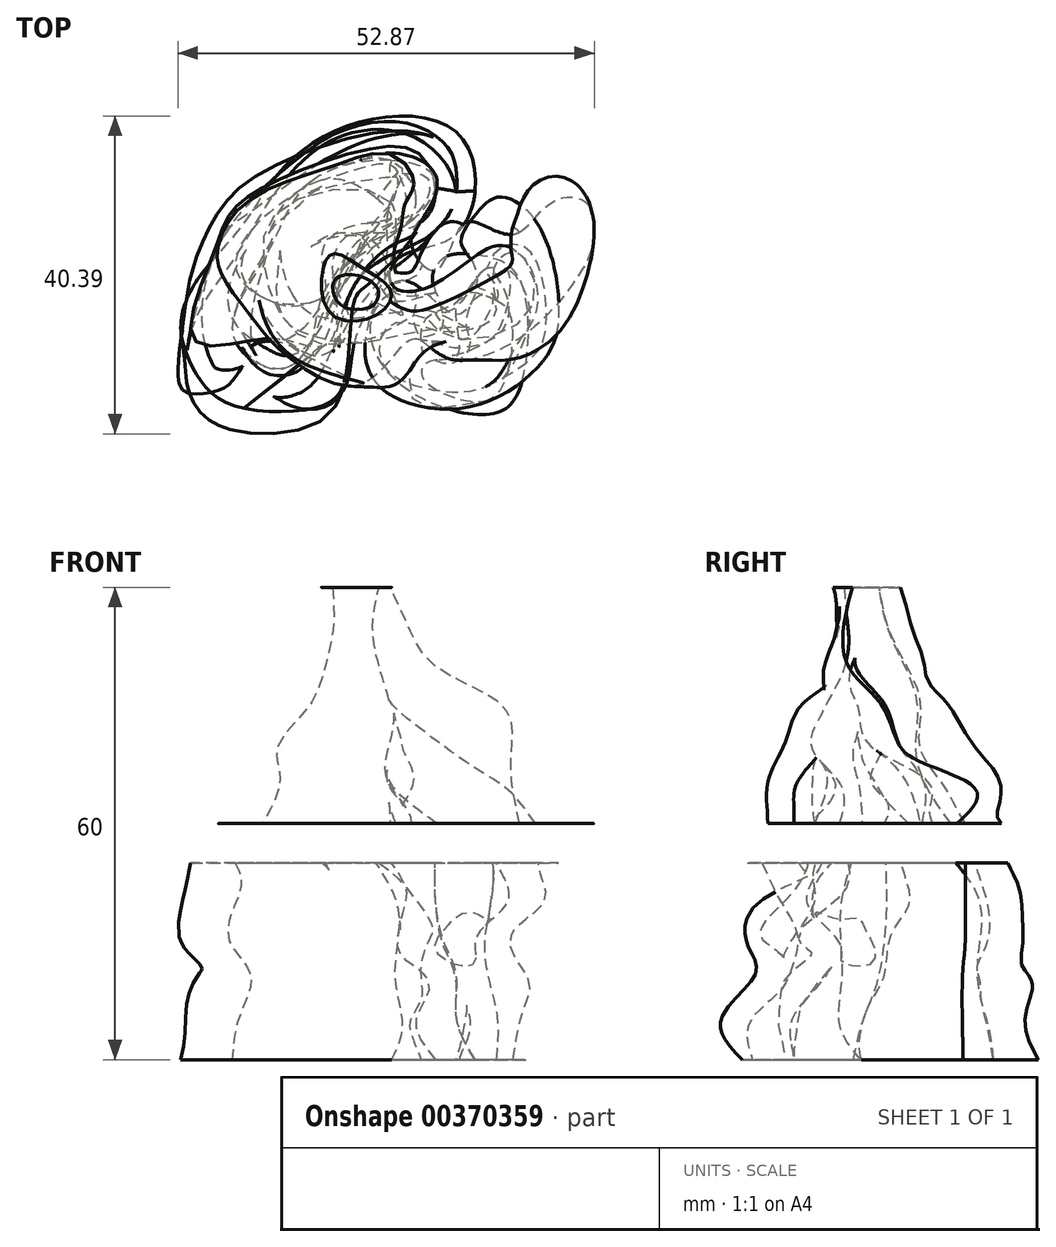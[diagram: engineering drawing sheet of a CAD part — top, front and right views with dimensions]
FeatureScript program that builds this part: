
annotation { "Feature Type Name" : "Feature", "Feature Type Description" : "" }
export const myFeature = defineFeature(function(context is Context, id is Id, definition is map)
    precondition{}
    {
        {
            var Q0;
            Q0=qCreatedBy(makeId("Top.planeOp"),FACE);
            cPlane(context, id + "F0", {"entities" : qUnion([Q0]), "cplaneType" : CPlaneType.OFFSET, "offset" : 5 * mm, "width" : 152.4 * mm, "height" : 152.4 * mm});
        }
        {
            var Q0;
            Q0=qCreatedBy(id+"F0.planeOp",FACE);
            var sketch = newSketch(context, id + "F1", { "sketchPlane" : qUnion([Q0])});
            skFitSpline(sketch, "E0", {"points": [v(10.66, 15.7) * mm, v(7.94, 23.44) * mm, v(-3.49, 24.6) * mm, v(-13.56, 18.8) * mm, v(-19.18, 11.04) * mm, v(-24.6, 4.46) * mm, v(-26.73, -1.55) * mm, v(-25, -7.17) * mm, v(-20.34, -11.43) * mm, v(-8.91, -11.62) * mm, v(-5.81, -7.94) * mm, v(-4.65, 1.94) * mm, v(-3.1, 3.68) * mm, v(1.55, 7.56) * mm, v(7.56, 9.69) * mm, v(10.66, 15.7) * mm]});
            skSolve(sketch);
        }
        {
            var Q0;
            Q0=qCreatedBy(id+"F0.planeOp",FACE);
            var sketch = newSketch(context, id + "F2", { "sketchPlane" : qUnion([Q0])});
            skFitSpline(sketch, "E1", {"points": [v(0, 2.71) * mm, v(-2.71, -1.94) * mm, v(1.74, -9.3) * mm, v(12.98, -12.6) * mm, v(16.66, -8.33) * mm, v(16.66, 3.68) * mm, v(13.95, 6.78) * mm, v(10.85, 7.56) * mm, v(6.97, 7.36) * mm, v(5.23, 4.84) * mm, v(6, 1.94) * mm, v(6.4, -1.74) * mm, v(4.84, -2.71) * mm, v(3.68, -2.71) * mm, v(2.9, 0) * mm, v(3.1, 2.71) * mm, v(0, 2.71) * mm]});
            skSolve(sketch);
        }
        {
            var Q0;
            Q0=qCreatedBy(id+"F0.planeOp",FACE);
            var sketch = newSketch(context, id + "F3", { "sketchPlane" : qUnion([Q0])});
            skFitSpline(sketch, "E2", {"points": [v(0, 19.57) * mm, v(-10.46, 16.66) * mm, v(-15.7, 7.94) * mm, v(-20.15, -2.32) * mm, v(-15.5, -6.78) * mm, v(-11.82, -5.81) * mm, v(-8.72, 0) * mm, v(-4.26, 8.14) * mm, v(2.13, 11.62) * mm, v(5.62, 17.05) * mm, v(0, 19.57) * mm]});
            skSolve(sketch);
        }
        {
            var Q0;
            Q0=qCreatedBy(id+"F0.planeOp",FACE);
            var sketch = newSketch(context, id + "F4", { "sketchPlane" : qUnion([Q0])});
            skFitSpline(sketch, "E3", {"points": [v(13.37, 1.74) * mm, v(9.5, 2.71) * mm, v(8.14, 0) * mm, v(8.33, -5.23) * mm, v(4.84, -6) * mm, v(3.87, -7.75) * mm, v(8.33, -10.66) * mm, v(12.98, -10.46) * mm, v(15.11, -6) * mm, v(15.11, 0) * mm, v(13.37, 1.74) * mm]});
            skSolve(sketch);
        }
        {
            var Q0;
            Q0=qCreatedBy(id+"F0.planeOp",FACE);
            cPlane(context, id + "F5", {"entities" : qUnion([Q0]), "cplaneType" : CPlaneType.OFFSET, "offset" : 5 * mm, "width" : 152.4 * mm, "height" : 152.4 * mm});
        }
        {
            var Q0;
            Q0=qCreatedBy(id+"F5.planeOp",FACE);
            var sketch = newSketch(context, id + "F6", { "sketchPlane" : qUnion([Q0])});
            skFitSpline(sketch, "E4", {"points": [v(3.1, 22.47) * mm, v(-6.78, 22.47) * mm, v(-14.14, 16.27) * mm, v(-20.15, 6.97) * mm, v(-24.6, 0) * mm, v(-25.96, -8.72) * mm, v(-21.31, -14.34) * mm, v(-8.91, -13.17) * mm, v(-6.78, -6.2) * mm, v(-4.07, 4.46) * mm, v(3.68, 9.3) * mm, v(8.33, 15.3) * mm, v(3.1, 22.47) * mm]});
            skSolve(sketch);
        }
        {
            var Q0;
            Q0=qCreatedBy(id+"F5.planeOp",FACE);
            var sketch = newSketch(context, id + "F7", { "sketchPlane" : qUnion([Q0])});
            skFitSpline(sketch, "E5", {"points": [v(1.74, 0) * mm, v(4.65, -1.74) * mm, v(8.91, 1.94) * mm, v(8.72, 9.3) * mm, v(12.6, 10.85) * mm, v(18.6, 9.5) * mm, v(20.54, 4.84) * mm, v(19.37, 0) * mm, v(16.47, -7.36) * mm, v(13.95, -9.88) * mm, v(6.4, -13.17) * mm, v(2.9, -12.6) * mm, v(0, -11.04) * mm, v(-1.94, -4.65) * mm, v(0, -1.74) * mm, v(1.74, 0) * mm]});
            skSolve(sketch);
        }
        {
            var Q0;
            Q0=qCreatedBy(id+"F5.planeOp",FACE);
            var sketch = newSketch(context, id + "F8", { "sketchPlane" : qUnion([Q0])});
            skFitSpline(sketch, "E6", {"points": [v(-1.95, 18.75) * mm, v(-12.28, 15.24) * mm, v(-14.78, 10.42) * mm, v(-18.5, 3.1) * mm, v(-19.3, -2.81) * mm, v(-16.29, -7.23) * mm, v(-12.38, -7.43) * mm, v(-10.17, -4.72) * mm, v(-8.97, 1.8) * mm, v(-4.46, 7.41) * mm, v(2.56, 12.43) * mm, v(2.56, 16.84) * mm, v(-1.95, 18.75) * mm]});
            skSolve(sketch);
        }
        {
            var Q0;
            Q0=qCreatedBy(id+"F5.planeOp",FACE);
            var sketch = newSketch(context, id + "F9", { "sketchPlane" : qUnion([Q0])});
            skFitSpline(sketch, "E7", {"points": [v(13.5, 3) * mm, v(10.59, 2) * mm, v(9.38, -0.9) * mm, v(9.99, -4.12) * mm, v(6.88, -6.02) * mm, v(4.47, -5.32) * mm, v(2.87, -5.82) * mm, v(2.46, -7.73) * mm, v(3.17, -10.84) * mm, v(9.58, -10.23) * mm, v(15.71, -5.86) * mm, v(15.71, 1.14) * mm, v(13.5, 3) * mm]});
            skSolve(sketch);
        }
        {
            var Q0;
            Q0=qCreatedBy(id+"F5.planeOp",FACE);
            cPlane(context, id + "F10", {"entities" : qUnion([Q0]), "cplaneType" : CPlaneType.OFFSET, "offset" : 5 * mm, "width" : 152.4 * mm, "height" : 152.4 * mm});
        }
        {
            var Q0;
            Q0=qCreatedBy(id+"F10.planeOp",FACE);
            var sketch = newSketch(context, id + "F11", { "sketchPlane" : qUnion([Q0])});
            skFitSpline(sketch, "E8", {"points": [v(-8.91, 21.9) * mm, v(2.9, 24.02) * mm, v(7.75, 19.95) * mm, v(7.17, 12.6) * mm, v(0, 5.62) * mm, v(-3.1, 2.32) * mm, v(-6.97, -3.49) * mm, v(-10.46, -9.5) * mm, v(-18.21, -11.04) * mm, v(-24.4, -7.17) * mm, v(-24.02, 2.9) * mm, v(-21.9, 8.91) * mm, v(-19.57, 12.2) * mm, v(-8.91, 21.9) * mm]});
            skSolve(sketch);
        }
        {
            var Q0;
            Q0=qCreatedBy(id+"F10.planeOp",FACE);
            var sketch = newSketch(context, id + "F12", { "sketchPlane" : qUnion([Q0])});
            skFitSpline(sketch, "E9", {"points": [v(0, -2.13) * mm, v(1.74, 2.13) * mm, v(3.87, 2.52) * mm, v(7.36, 2.13) * mm, v(9.88, 5.81) * mm, v(12.98, 7.56) * mm, v(16.85, 6.97) * mm, v(18.21, 3.1) * mm, v(18.4, -1.55) * mm, v(16.27, -4.84) * mm, v(12.2, -6.97) * mm, v(8.91, -7.75) * mm, v(4.26, -8.14) * mm, v(1.55, -5.62) * mm, v(0, -2.13) * mm]});
            skSolve(sketch);
        }
        {
            var Q0;
            Q0=qCreatedBy(id+"F10.planeOp",FACE);
            var sketch = newSketch(context, id + "F13", { "sketchPlane" : qUnion([Q0])});
            skFitSpline(sketch, "E10", {"points": [v(14.7, 5.4) * mm, v(11.29, 4) * mm, v(10.09, 2.3) * mm, v(6.68, -2.41) * mm, v(4.17, -2.31) * mm, v(3.87, -4.02) * mm, v(6.07, -6.32) * mm, v(13.6, -5.72) * mm, v(16.9, -2.41) * mm, v(17.4, 1.7) * mm, v(14.7, 5.4) * mm]});
            skSolve(sketch);
        }
        {
            var Q0;
            Q0=qCreatedBy(id+"F10.planeOp",FACE);
            var sketch = newSketch(context, id + "F14", { "sketchPlane" : qUnion([Q0])});
            skFitSpline(sketch, "E11", {"points": [v(-0.95, 17.44) * mm, v(-13.38, 14.13) * mm, v(-15.29, 9.52) * mm, v(-17.8, -1.1) * mm, v(-15.49, -6.93) * mm, v(-8.77, -3.01) * mm, v(-5.46, 7.72) * mm, v(0, 11.53) * mm, v(3.87, 13.93) * mm, v(4.57, 17.24) * mm, v(-0.95, 17.44) * mm]});
            skSolve(sketch);
        }
        {
            var Q0;
            Q0=qCreatedBy(id+"F10.planeOp",FACE);
            cPlane(context, id + "F15", {"entities" : qUnion([Q0]), "cplaneType" : CPlaneType.OFFSET, "offset" : 5 * mm, "width" : 152.4 * mm, "height" : 152.4 * mm});
        }
        {
            var Q0;
            Q0=qCreatedBy(id+"F15.planeOp",FACE);
            var sketch = newSketch(context, id + "F16", { "sketchPlane" : qUnion([Q0])});
            skFitSpline(sketch, "E12", {"points": [v(-17.05, 13.75) * mm, v(-5.81, 21.31) * mm, v(5.62, 21.9) * mm, v(4.84, 11.82) * mm, v(0, 8.72) * mm, v(-4.65, 3.68) * mm, v(-7.17, -3.87) * mm, v(-8.14, -10.07) * mm, v(-10.07, -11.62) * mm, v(-13.17, -11.43) * mm, v(-15.3, -8.91) * mm, v(-15.89, -6.78) * mm, v(-18.6, -6.4) * mm, v(-20.54, -8.52) * mm, v(-22.09, -9.3) * mm, v(-25.18, -9.5) * mm, v(-26.54, -8.72) * mm, v(-26.35, -2.71) * mm, v(-24.22, 7.36) * mm, v(-17.05, 13.75) * mm]});
            skSolve(sketch);
        }
        {
            var Q0;
            Q0=qCreatedBy(id+"F15.planeOp",FACE);
            var sketch = newSketch(context, id + "F17", { "sketchPlane" : qUnion([Q0])});
            skFitSpline(sketch, "E13", {"points": [v(0, 18.6) * mm, v(-12.7, 13.89) * mm, v(-15.9, 9.73) * mm, v(-20.33, 2.38) * mm, v(-19.78, -1.22) * mm, v(-16.31, -4) * mm, v(-11.74, -4.68) * mm, v(-4.67, 7.23) * mm, v(0, 14.02) * mm, v(0, 18.6) * mm]});
            skSolve(sketch);
        }
        {
            var Q0;
            Q0=qCreatedBy(id+"F15.planeOp",FACE);
            var sketch = newSketch(context, id + "F18", { "sketchPlane" : qUnion([Q0])});
            skFitSpline(sketch, "E14", {"points": [v(14.6, 5.85) * mm, v(11.4, 5.3) * mm, v(9.32, 1.83) * mm, v(5.72, 0) * mm, v(4.75, -3.02) * mm, v(6.7, -5.24) * mm, v(11.54, -3.85) * mm, v(13.9, -1.5) * mm, v(14.6, 5.85) * mm]});
            skSolve(sketch);
        }
        {
            var Q0;
            Q0=qCreatedBy(id+"F15.planeOp",FACE);
            cPlane(context, id + "F19", {"entities" : qUnion([Q0]), "cplaneType" : CPlaneType.OFFSET, "offset" : 5 * mm, "width" : 152.4 * mm, "height" : 152.4 * mm});
        }
        {
            var Q0;
            Q0=qCreatedBy(id+"F19.planeOp",FACE);
            var sketch = newSketch(context, id + "F20", { "sketchPlane" : qUnion([Q0])});
            skFitSpline(sketch, "E15", {"points": [v(0, -2.9) * mm, v(2.13, 2.32) * mm, v(6.97, -1.74) * mm, v(10.27, -2.71) * mm, v(13.17, 2.32) * mm, v(11.62, 3.49) * mm, v(8.78, 5.55) * mm, v(7.73, 7.13) * mm, v(10.2, 11.79) * mm, v(15.4, 12.24) * mm, v(18.99, 10.07) * mm, v(21.31, 3.87) * mm, v(21.5, -4.26) * mm, v(17.24, -7.75) * mm, v(10.46, -8.72) * mm, v(3.68, -8.72) * mm, v(0, -7.56) * mm, v(0, -2.9) * mm]});
            skSolve(sketch);
        }
        {
            var Q0;
            Q0=qCreatedBy(id+"F19.planeOp",FACE);
            var sketch = newSketch(context, id + "F21", { "sketchPlane" : qUnion([Q0])});
            skFitSpline(sketch, "E16", {"points": [v(-25.96, -5.81) * mm, v(-22.09, -6.97) * mm, v(-18.6, -4.84) * mm, v(-16.47, -3.3) * mm, v(-13.37, -3.87) * mm, v(-12.79, -6.4) * mm, v(-11.82, -9.3) * mm, v(-7.56, -10.07) * mm, v(-5.42, -7.94) * mm, v(-4.65, -3.3) * mm, v(0, 6) * mm, v(1.55, 8.33) * mm, v(5.62, 15.89) * mm, v(2.32, 22.28) * mm, v(-4.26, 22.67) * mm, v(-15.5, 18.21) * mm, v(-22.09, 12.79) * mm, v(-25.57, 2.71) * mm, v(-25.96, -5.81) * mm]});
            skSolve(sketch);
        }
        {
            var Q0;
            Q0=qCreatedBy(id+"F19.planeOp",FACE);
            var sketch = newSketch(context, id + "F22", { "sketchPlane" : qUnion([Q0])});
            skFitSpline(sketch, "E17", {"points": [v(0, 18.32) * mm, v(-8.7, 16.52) * mm, v(-12.3, 13.47) * mm, v(-17.28, 9.87) * mm, v(-19.5, 3.08) * mm, v(-14.37, 0) * mm, v(-8.7, 0) * mm, v(-3.15, 9.17) * mm, v(1.56, 13.05) * mm, v(0, 18.32) * mm]});
            skSolve(sketch);
        }
        {
            var Q0;
            Q0=qCreatedBy(id+"F19.planeOp",FACE);
            var sketch = newSketch(context, id + "F23", { "sketchPlane" : qUnion([Q0])});
            skFitSpline(sketch, "E18", {"points": [v(12.65, 7.1) * mm, v(13.9, 3.9) * mm, v(14.73, 0) * mm, v(13.2, -2.6) * mm, v(7.8, -4.13) * mm, v(5.44, -3.44) * mm, v(3.78, -4.13) * mm, v(3.92, -6.62) * mm, v(16.8, -5.52) * mm, v(19.44, 0) * mm, v(16.4, 8.76) * mm, v(12.65, 7.1) * mm]});
            skSolve(sketch);
        }
        {
            var Q0;
            Q0=qCreatedBy(id+"F19.planeOp",FACE);
            cPlane(context, id + "F24", {"entities" : qUnion([Q0]), "cplaneType" : CPlaneType.OFFSET, "offset" : 5 * mm, "width" : 152.4 * mm, "height" : 152.4 * mm});
        }
        {
            var Q0;
            Q0=qCreatedBy(id+"F24.planeOp",FACE);
            var sketch = newSketch(context, id + "F25", { "sketchPlane" : qUnion([Q0])});
            skFitSpline(sketch, "E19", {"points": [v(-25, -3.3) * mm, v(-16.66, -3.1) * mm, v(-12.79, -3.68) * mm, v(-9.5, -5.23) * mm, v(-5.62, -2.71) * mm, v(-5.42, 0) * mm, v(-6.97, 3.3) * mm, v(-7.36, 6.78) * mm, v(-6, 9.69) * mm, v(-3.68, 10.46) * mm, v(0, 10.46) * mm, v(5.04, 13.17) * mm, v(4.07, 19.95) * mm, v(-2.32, 21.12) * mm, v(-15.3, 16.66) * mm, v(-20.34, 12.98) * mm, v(-22.67, 7.56) * mm, v(-25, -3.3) * mm]});
            skSolve(sketch);
        }
        {
            var Q0;
            Q0=qCreatedBy(id+"F24.planeOp",FACE);
            var sketch = newSketch(context, id + "F26", { "sketchPlane" : qUnion([Q0])});
            skFitSpline(sketch, "E20", {"points": [v(2.9, 3.87) * mm, v(0, 3.87) * mm, v(-2.09, 1.21) * mm, v(-3.3, -5.42) * mm, v(0, -10.27) * mm, v(10.46, -11.62) * mm, v(19.18, -6) * mm, v(21.31, 0) * mm, v(18.4, 11.82) * mm, v(13.56, 14.92) * mm, v(10.66, 12.61) * mm, v(8.86, 9.23) * mm, v(10.46, 6.4) * mm, v(10.46, 2.13) * mm, v(8.14, 0) * mm, v(2.9, 3.87) * mm]});
            skSolve(sketch);
        }
        {
            var Q0;
            Q0=qCreatedBy(id+"F24.planeOp",FACE);
            var sketch = newSketch(context, id + "F27", { "sketchPlane" : qUnion([Q0])});
            skFitSpline(sketch, "E21", {"points": [v(-6.2, 17.07) * mm, v(-12.7, 15) * mm, v(-17.56, 10.98) * mm, v(-19.64, 5.3) * mm, v(-14.1, 1.28) * mm, v(-11.18, 1.28) * mm, v(-8.41, 2.8) * mm, v(-8.7, 8.2) * mm, v(-3.84, 11.53) * mm, v(0, 12.36) * mm, v(-6.2, 17.07) * mm]});
            skSolve(sketch);
        }
        {
            var Q0;
            Q0=qCreatedBy(id+"F24.planeOp",FACE);
            var sketch = newSketch(context, id + "F28", { "sketchPlane" : qUnion([Q0])});
            skFitSpline(sketch, "E22", {"points": [v(15.98, 7.79) * mm, v(12.93, 5.57) * mm, v(13.2, 0) * mm, v(10.02, -1.91) * mm, v(5.72, -2.05) * mm, v(0, -1.22) * mm, v(-1.48, -5.24) * mm, v(2.12, -8.7) * mm, v(12.1, -9.12) * mm, v(15.84, -4) * mm, v(18.6, 1.28) * mm, v(15.98, 7.79) * mm]});
            skSolve(sketch);
        }
        {
            var Q0;
            Q0=qCreatedBy(id+"F24.planeOp",FACE);
            cPlane(context, id + "F29", {"entities" : qUnion([Q0]), "cplaneType" : CPlaneType.OFFSET, "offset" : 5 * mm, "width" : 152.4 * mm, "height" : 152.4 * mm});
        }
        {
            var Q0;
            Q0=qCreatedBy(id+"F29.planeOp",FACE);
            var sketch = newSketch(context, id + "F30", { "sketchPlane" : qUnion([Q0])});
            skFitSpline(sketch, "E23", {"points": [v(16.27, 10.46) * mm, v(20.54, 14.34) * mm, v(24.8, 14.14) * mm, v(25.57, 8.91) * mm, v(23.44, 4.46) * mm, v(17.24, -2.32) * mm, v(7.36, -5.62) * mm, v(3.1, -3.1) * mm, v(0, -5.62) * mm, v(-5.23, -9.1) * mm, v(-14.14, -4.46) * mm, v(-18.02, 0) * mm, v(-21.31, 4.65) * mm, v(-22.09, 7.94) * mm, v(-18.02, 14.53) * mm, v(-3.49, 19.76) * mm, v(0, 20.54) * mm, v(5.23, 18.4) * mm, v(5.04, 13.95) * mm, v(2.52, 9.3) * mm, v(5.42, 5.62) * mm, v(8.14, 9.88) * mm, v(9.88, 11.82) * mm, v(13.17, 10.66) * mm, v(16.27, 10.46) * mm]});
            skSolve(sketch);
        }
        {
            var Q0;
            Q0=qCreatedBy(id+"F29.planeOp",FACE);
            var sketch = newSketch(context, id + "F31", { "sketchPlane" : qUnion([Q0])});
            skFitSpline(sketch, "E24", {"points": [v(0, 14.16) * mm, v(-13.54, 13.75) * mm, v(-16.17, 6.13) * mm, v(-11.46, -2.74) * mm, v(-1.48, -2.6) * mm, v(3.78, 0) * mm, v(7.1, -2.74) * mm, v(17.36, 0) * mm, v(16.95, 7.1) * mm, v(12.93, 8.62) * mm, v(5.03, 3.63) * mm, v(0, 4.05) * mm, v(0, 14.16) * mm]});
            skSolve(sketch);
        }
        {
            var Q0;
            Q0=qCreatedBy(id+"F29.planeOp",FACE);
            cPlane(context, id + "F32", {"entities" : qUnion([Q0]), "cplaneType" : CPlaneType.OFFSET, "offset" : 5 * mm, "width" : 152.4 * mm, "height" : 152.4 * mm});
        }
        {
            var Q0;
            Q0=qCreatedBy(id+"F32.planeOp",FACE);
            var sketch = newSketch(context, id + "F33", { "sketchPlane" : qUnion([Q0])});
            skFitSpline(sketch, "E25", {"points": [v(-6.97, 17.82) * mm, v(-15.89, 14.34) * mm, v(-18.4, 7.36) * mm, v(-17.63, 0) * mm, v(-10.66, -5.42) * mm, v(-10.07, -5.62) * mm, v(-1.94, -9.1) * mm, v(1.94, -7.56) * mm, v(4.26, -4.65) * mm, v(8.14, -3.49) * mm, v(13.37, -5.42) * mm, v(19.76, -3.3) * mm, v(23.44, 2.9) * mm, v(24.4, 10.07) * mm, v(21.7, 16.08) * mm, v(18.02, 16.08) * mm, v(15.7, 11.82) * mm, v(14.14, 8.91) * mm, v(11.82, 8.72) * mm, v(10.07, 9.69) * mm, v(6.78, 11.43) * mm, v(3.68, 6.78) * mm, v(3.3, 5.04) * mm, v(0, 4.26) * mm, v(0, 7.56) * mm, v(0, 14.53) * mm, v(2.71, 16.66) * mm, v(0, 20.34) * mm, v(-6.97, 17.82) * mm]});
            skSolve(sketch);
        }
        {
            var Q0;
            Q0=qCreatedBy(id+"F32.planeOp",FACE);
            var sketch = newSketch(context, id + "F34", { "sketchPlane" : qUnion([Q0])});
            skFitSpline(sketch, "E26", {"points": [v(-2.18, 10.14) * mm, v(-12.3, 12.64) * mm, v(-14.1, 7.51) * mm, v(-10.08, 0) * mm, v(3.92, 0) * mm, v(11.13, -1.36) * mm, v(13.76, 3.9) * mm, v(10.16, 4.46) * mm, v(4.9, 2.94) * mm, v(0, 3.08) * mm, v(-2.18, 10.14) * mm]});
            skSolve(sketch);
        }
        {
            var Q0;
            Q0=qCreatedBy(id+"F32.planeOp",FACE);
            cPlane(context, id + "F35", {"entities" : qUnion([Q0]), "cplaneType" : CPlaneType.OFFSET, "offset" : 5 * mm, "width" : 152.4 * mm, "height" : 152.4 * mm});
        }
        {
            var Q0;
            Q0=qCreatedBy(id+"F35.planeOp",FACE);
            var sketch = newSketch(context, id + "F36", { "sketchPlane" : qUnion([Q0])});
            skFitSpline(sketch, "E27", {"points": [v(-15.11, 12.79) * mm, v(-10.27, 15.11) * mm, v(-2.32, 16.66) * mm, v(0, 16.66) * mm, v(1.36, 12.01) * mm, v(0, 8.33) * mm, v(0, 5.81) * mm, v(1.74, 5.04) * mm, v(4.84, 3.87) * mm, v(10.07, 4.84) * mm, v(13.75, 7.36) * mm, v(18.8, 6) * mm, v(18.21, 0) * mm, v(14.72, -2.32) * mm, v(8.72, -2.52) * mm, v(6.2, -1.94) * mm, v(2.32, -3.1) * mm, v(0, -5.42) * mm, v(-8.91, -6.78) * mm, v(-16.27, 0) * mm, v(-15.11, 12.79) * mm]});
            skSolve(sketch);
        }
        {
            var Q0;
            Q0=qCreatedBy(id+"F35.planeOp",FACE);
            var sketch = newSketch(context, id + "F37", { "sketchPlane" : qUnion([Q0])});
            skFitSpline(sketch, "E28", {"points": [v(-4.4, 10) * mm, v(-12.3, 7.51) * mm, v(-13.82, 0) * mm, v(-8.27, -3.16) * mm, v(-1.48, -3.16) * mm, v(3.92, 0) * mm, v(6.41, 1.28) * mm, v(4.9, 2.52) * mm, v(0, 1.97) * mm, v(-2.32, 7.23) * mm, v(-4.4, 10) * mm]});
            skSolve(sketch);
        }
        {
            var Q0;
            Q0=qCreatedBy(id+"F35.planeOp",FACE);
            cPlane(context, id + "F38", {"entities" : qUnion([Q0]), "cplaneType" : CPlaneType.OFFSET, "offset" : 5 * mm, "width" : 152.4 * mm, "height" : 152.4 * mm});
        }
        {
            var Q0;
            Q0=qCreatedBy(id+"F38.planeOp",FACE);
            var sketch = newSketch(context, id + "F39", { "sketchPlane" : qUnion([Q0])});
            skFitSpline(sketch, "E29", {"points": [v(-3.49, 13.56) * mm, v(-12.01, 11.82) * mm, v(-12.98, 5.81) * mm, v(-9.1, -2.52) * mm, v(-4.26, -4.84) * mm, v(0, -2.52) * mm, v(10.07, -1.74) * mm, v(16.47, 1.74) * mm, v(12.79, 5.81) * mm, v(6.4, 2.71) * mm, v(1.36, 3.3) * mm, v(0, 9.1) * mm, v(-3.49, 13.56) * mm]});
            skSolve(sketch);
        }
        {
            var Q0;
            Q0=qCreatedBy(id+"F38.planeOp",FACE);
            var sketch = newSketch(context, id + "F40", { "sketchPlane" : qUnion([Q0])});
            skFitSpline(sketch, "E30", {"points": [v(-1.76, 8.76) * mm, v(-8.55, 9.73) * mm, v(-10.21, 4.32) * mm, v(-5.36, -1.64) * mm, v(0, 0) * mm, v(0, 2.25) * mm, v(-1.76, 8.76) * mm]});
            skSolve(sketch);
        }
        {
            var Q0;
            Q0=qCreatedBy(id+"F38.planeOp",FACE);
            cPlane(context, id + "F41", {"entities" : qUnion([Q0]), "cplaneType" : CPlaneType.OFFSET, "offset" : 5 * mm, "width" : 152.4 * mm, "height" : 152.4 * mm});
        }
        {
            var Q0;
            Q0=qCreatedBy(id+"F41.planeOp",FACE);
            var sketch = newSketch(context, id + "F42", { "sketchPlane" : qUnion([Q0])});
            skFitSpline(sketch, "E31", {"points": [v(-2.32, 9.5) * mm, v(-9.88, 10.07) * mm, v(-10.07, 3.49) * mm, v(-6.78, 0) * mm, v(0, -1.94) * mm, v(5.62, 0) * mm, v(4.46, 1.94) * mm, v(0, 1.55) * mm, v(0, 2.13) * mm, v(0, 6.2) * mm, v(-2.32, 9.5) * mm]});
            skSolve(sketch);
        }
        {
            var Q0;
            Q0=qCreatedBy(id+"F41.planeOp",FACE);
            var sketch = newSketch(context, id + "F43", { "sketchPlane" : qUnion([Q0])});
            skFitSpline(sketch, "E32", {"points": [v(-3.14, 7.61) * mm, v(-7.34, 7.94) * mm, v(-8.33, 4.32) * mm, v(-7.1, 2.17) * mm, v(-3.22, 0.7) * mm, v(-1.66, 2.26) * mm, v(-3.14, 7.61) * mm]});
            skSolve(sketch);
        }
        {
            var Q0;
            Q0=qCreatedBy(id+"F41.planeOp",FACE);
            cPlane(context, id + "F44", {"entities" : qUnion([Q0]), "cplaneType" : CPlaneType.OFFSET, "offset" : 5 * mm, "width" : 152.4 * mm, "height" : 152.4 * mm});
        }
        {
            var Q0;
            Q0=qCreatedBy(id+"F44.planeOp",FACE);
            var sketch = newSketch(context, id + "F45", { "sketchPlane" : qUnion([Q0])});
            skFitSpline(sketch, "E33", {"points": [v(-1.74, 5.23) * mm, v(-5.04, 8.72) * mm, v(-9.88, 7.56) * mm, v(-6.2, 0) * mm, v(-2.52, 0) * mm, v(2.13, 0) * mm, v(0, 3.87) * mm, v(-1.74, 5.23) * mm]});
            skSolve(sketch);
        }
        {
            var Q0;
            Q0=qCreatedBy(id+"F44.planeOp",FACE);
            var sketch = newSketch(context, id + "F46", { "sketchPlane" : qUnion([Q0])});
            skFitSpline(sketch, "E34", {"points": [v(-2.81, 4.23) * mm, v(-5.78, 6.13) * mm, v(-7.34, 3.99) * mm, v(-5.28, 1.35) * mm, v(-2.73, 1.51) * mm, v(-2.81, 4.23) * mm]});
            skSolve(sketch);
        }
        {
            var Q0;
            Q0=qCreatedBy(id+"F44.planeOp",FACE);
            cPlane(context, id + "F47", {"entities" : qUnion([Q0]), "cplaneType" : CPlaneType.OFFSET, "offset" : 5 * mm, "width" : 152.4 * mm, "height" : 152.4 * mm});
        }
        {
            var Q0;
            Q0=qCreatedBy(id+"F47.planeOp",FACE);
            var sketch = newSketch(context, id + "F48", { "sketchPlane" : qUnion([Q0])});
            skFitSpline(sketch, "E35", {"points": [v(-3.49, 5.81) * mm, v(-7.36, 7.75) * mm, v(-8.72, 5.62) * mm, v(-7.56, 0) * mm, v(-1.74, 0) * mm, v(0, 2.9) * mm, v(-3.49, 5.81) * mm]});
            skSolve(sketch);
        }
        {
            var Q0;
            Q0=qCreatedBy(id+"F47.planeOp",FACE);
            var sketch = newSketch(context, id + "F49", { "sketchPlane" : qUnion([Q0])});
            skFitSpline(sketch, "E36", {"points": [v(-4.87, 5.06) * mm, v(-7.26, 4.32) * mm, v(-7.18, 2.26) * mm, v(-5.53, 0.77) * mm, v(-2.32, 1.18) * mm, v(-1.74, 3.33) * mm, v(-4.87, 5.06) * mm]});
            skSolve(sketch);
        }
        {
            var Q0;
            Q0=makeQuery(id+"F30.imprint","IMPRINT",FACE,{"disambiguationData":[TD([[makeQuery(id+"F30.imprint","IMPRINT",EDGE,{"derivedFrom":sQuery(id+"F30.wireOp",EDGE,"E23")}),-1.0]])]});
            var Q1;
            Q1=makeQuery(id+"F33.imprint","IMPRINT",FACE,{"disambiguationData":[TD([[makeQuery(id+"F33.imprint","IMPRINT",EDGE,{"derivedFrom":sQuery(id+"F33.wireOp",EDGE,"E25")}),1.0]])]});
            var Q2;
            Q2=makeQuery(id+"F36.imprint","IMPRINT",FACE,{"disambiguationData":[TD([[makeQuery(id+"F36.imprint","IMPRINT",EDGE,{"derivedFrom":sQuery(id+"F36.wireOp",EDGE,"E27")}),-1.0]])]});
            var Q3;
            Q3=makeQuery(id+"F39.imprint","IMPRINT",FACE,{"disambiguationData":[TD([[makeQuery(id+"F39.imprint","IMPRINT",EDGE,{"derivedFrom":sQuery(id+"F39.wireOp",EDGE,"E29")}),1.0]])]});
            var Q4;
            Q4=makeQuery(id+"F42.imprint","IMPRINT",FACE,{"disambiguationData":[TD([[makeQuery(id+"F42.imprint","IMPRINT",EDGE,{"derivedFrom":sQuery(id+"F42.wireOp",EDGE,"E31")}),1.0]])]});
            var Q5;
            Q5=makeQuery(id+"F45.imprint","IMPRINT",FACE,{"disambiguationData":[TD([[makeQuery(id+"F45.imprint","IMPRINT",EDGE,{"derivedFrom":sQuery(id+"F45.wireOp",EDGE,"E33")}),1.0]])]});
            var Q6;
            Q6=makeQuery(id+"F48.imprint","IMPRINT",FACE,{"disambiguationData":[TD([[makeQuery(id+"F48.imprint","IMPRINT",EDGE,{"derivedFrom":sQuery(id+"F48.wireOp",EDGE,"E35")}),1.0]])]});
            loft(context, id + "F50", {"sheetProfilesArray" : [{ "sheetProfileEntities" : qUnion([Q0]) }, { "sheetProfileEntities" : qUnion([Q1]) }, { "sheetProfileEntities" : qUnion([Q2]) }, { "sheetProfileEntities" : qUnion([Q3]) }, { "sheetProfileEntities" : qUnion([Q4]) }, { "sheetProfileEntities" : qUnion([Q5]) }, { "sheetProfileEntities" : qUnion([Q6]) }]});
        }
        {
            var Q1;
            Q1 = qSketchRegion(id + "F31", true);
            var Q2;
            Q2 = qSketchRegion(id + "F34", true);
            var Q3;
            Q3 = qSketchRegion(id + "F37", true);
            var Q4;
            Q4 = qSketchRegion(id + "F40", true);
            var Q5;
            Q5 = qSketchRegion(id + "F43", true);
            var Q6;
            Q6 = qSketchRegion(id + "F46", true);
            var Q7;
            Q7 = qSketchRegion(id + "F49", true);
            loft(context, id + "F51", {"operationType" : NewBodyOperationType.REMOVE, "sheetProfilesArray" : [{ "sheetProfileEntities" : qUnion([Q1]) }, { "sheetProfileEntities" : qUnion([Q2]) }, { "sheetProfileEntities" : qUnion([Q3]) }, { "sheetProfileEntities" : qUnion([Q4]) }, { "sheetProfileEntities" : qUnion([Q5]) }, { "sheetProfileEntities" : qUnion([Q6]) }, { "sheetProfileEntities" : qUnion([Q7]) }]});
        }
        {
            var Q0;
            Q0 = qSketchRegion(id + "F1", true);
            var Q1;
            Q1 = qSketchRegion(id + "F6", true);
            var Q2;
            Q2 = qSketchRegion(id + "F11", true);
            var Q3;
            Q3 = qSketchRegion(id + "F16", true);
            var Q4;
            Q4 = qSketchRegion(id + "F21", true);
            var Q5;
            Q5 = qSketchRegion(id + "F25", true);
            loft(context, id + "F52", {"sheetProfilesArray" : [{ "sheetProfileEntities" : qUnion([Q0]) }, { "sheetProfileEntities" : qUnion([Q1]) }, { "sheetProfileEntities" : qUnion([Q2]) }, { "sheetProfileEntities" : qUnion([Q3]) }, { "sheetProfileEntities" : qUnion([Q4]) }, { "sheetProfileEntities" : qUnion([Q5]) }]});
        }
        {
            var Q1;
            Q1 = qSketchRegion(id + "F3", true);
            var Q2;
            Q2 = qSketchRegion(id + "F8", true);
            var Q3;
            Q3 = qSketchRegion(id + "F14", true);
            var Q4;
            Q4 = qSketchRegion(id + "F17", true);
            var Q5;
            Q5 = qSketchRegion(id + "F22", true);
            var Q6;
            Q6 = qSketchRegion(id + "F27", true);
            loft(context, id + "F53", {"operationType" : NewBodyOperationType.REMOVE, "sheetProfilesArray" : [{ "sheetProfileEntities" : qUnion([Q1]) }, { "sheetProfileEntities" : qUnion([Q2]) }, { "sheetProfileEntities" : qUnion([Q3]) }, { "sheetProfileEntities" : qUnion([Q4]) }, { "sheetProfileEntities" : qUnion([Q5]) }, { "sheetProfileEntities" : qUnion([Q6]) }]});
        }
        {
            var Q0;
            Q0=makeQuery(id+"F2.imprint","IMPRINT",FACE,{"disambiguationData":[TD([[makeQuery(id+"F2.imprint","IMPRINT",EDGE,{"derivedFrom":sQuery(id+"F2.wireOp",EDGE,"E1")}),1.0]])]});
            var Q1;
            Q1=makeQuery(id+"F7.imprint","IMPRINT",FACE,{"disambiguationData":[TD([[makeQuery(id+"F7.imprint","IMPRINT",EDGE,{"derivedFrom":sQuery(id+"F7.wireOp",EDGE,"E5")}),-1.0]])]});
            var Q2;
            Q2=makeQuery(id+"F12.imprint","IMPRINT",FACE,{"disambiguationData":[TD([[makeQuery(id+"F12.imprint","IMPRINT",EDGE,{"derivedFrom":sQuery(id+"F12.wireOp",EDGE,"E9")}),-1.0]])]});
            var Q3;
            Q3=makeQuery(id+"F20.imprint","IMPRINT",FACE,{"disambiguationData":[TD([[makeQuery(id+"F20.imprint","IMPRINT",EDGE,{"derivedFrom":sQuery(id+"F20.wireOp",EDGE,"E15")}),-1.0]])]});
            var Q4;
            Q4=makeQuery(id+"F26.imprint","IMPRINT",FACE,{"disambiguationData":[TD([[makeQuery(id+"F26.imprint","IMPRINT",EDGE,{"derivedFrom":sQuery(id+"F26.wireOp",EDGE,"E20")}),1.0]])]});
            loft(context, id + "F54", {"sheetProfilesArray" : [{ "sheetProfileEntities" : qUnion([Q0]) }, { "sheetProfileEntities" : qUnion([Q1]) }, { "sheetProfileEntities" : qUnion([Q2]) }, { "sheetProfileEntities" : qUnion([Q3]) }, { "sheetProfileEntities" : qUnion([Q4]) }]});
        }
        {
            var Q1;
            Q1 = qSketchRegion(id + "F4", true);
            var Q2;
            Q2 = qSketchRegion(id + "F9", true);
            var Q3;
            Q3 = qSketchRegion(id + "F13", true);
            var Q4;
            Q4 = qSketchRegion(id + "F18", true);
            var Q5;
            Q5 = qSketchRegion(id + "F23", true);
            var Q6;
            Q6 = qSketchRegion(id + "F28", true);
            loft(context, id + "F55", {"operationType" : NewBodyOperationType.REMOVE, "sheetProfilesArray" : [{ "sheetProfileEntities" : qUnion([Q1]) }, { "sheetProfileEntities" : qUnion([Q2]) }, { "sheetProfileEntities" : qUnion([Q3]) }, { "sheetProfileEntities" : qUnion([Q4]) }, { "sheetProfileEntities" : qUnion([Q5]) }, { "sheetProfileEntities" : qUnion([Q6]) }]});
        }
    });
